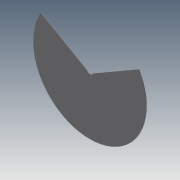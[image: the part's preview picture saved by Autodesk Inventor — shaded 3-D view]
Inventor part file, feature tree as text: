
AUTODESK INVENTOR PART (.ipt)
format: ipt  version: 2011 (Build 150239000, 239)  size: 76,800 bytes
history: native  units: in
note: dims shown in document units (in); Inventor stores cm internally (conversion verified against a paired STEP export)
features: extrude x1, sketch x1
ambient origin geometry x8: Origin, YZ Plane, XZ Plane, XY Plane, X Axis, Y Axis, Z Axis, Center Point
bodies: Solid1 (feature_tree)
feature tree (2):
  extrude  "Extrusion1"  TaperAngle=30.0deg  [1 undecoded]
  sketch  "Sketch1"  dims[d0=12.0in d1=30.0deg d2=150.0deg d3=0.25in d4=0.25in d5=0.0394in d6=0.0in]
note: 1 required parameter value undecoded (feature->parameter linkage not recoverable at this tier; creation-order binding heuristic only, values carry confidence <= 0.55)
